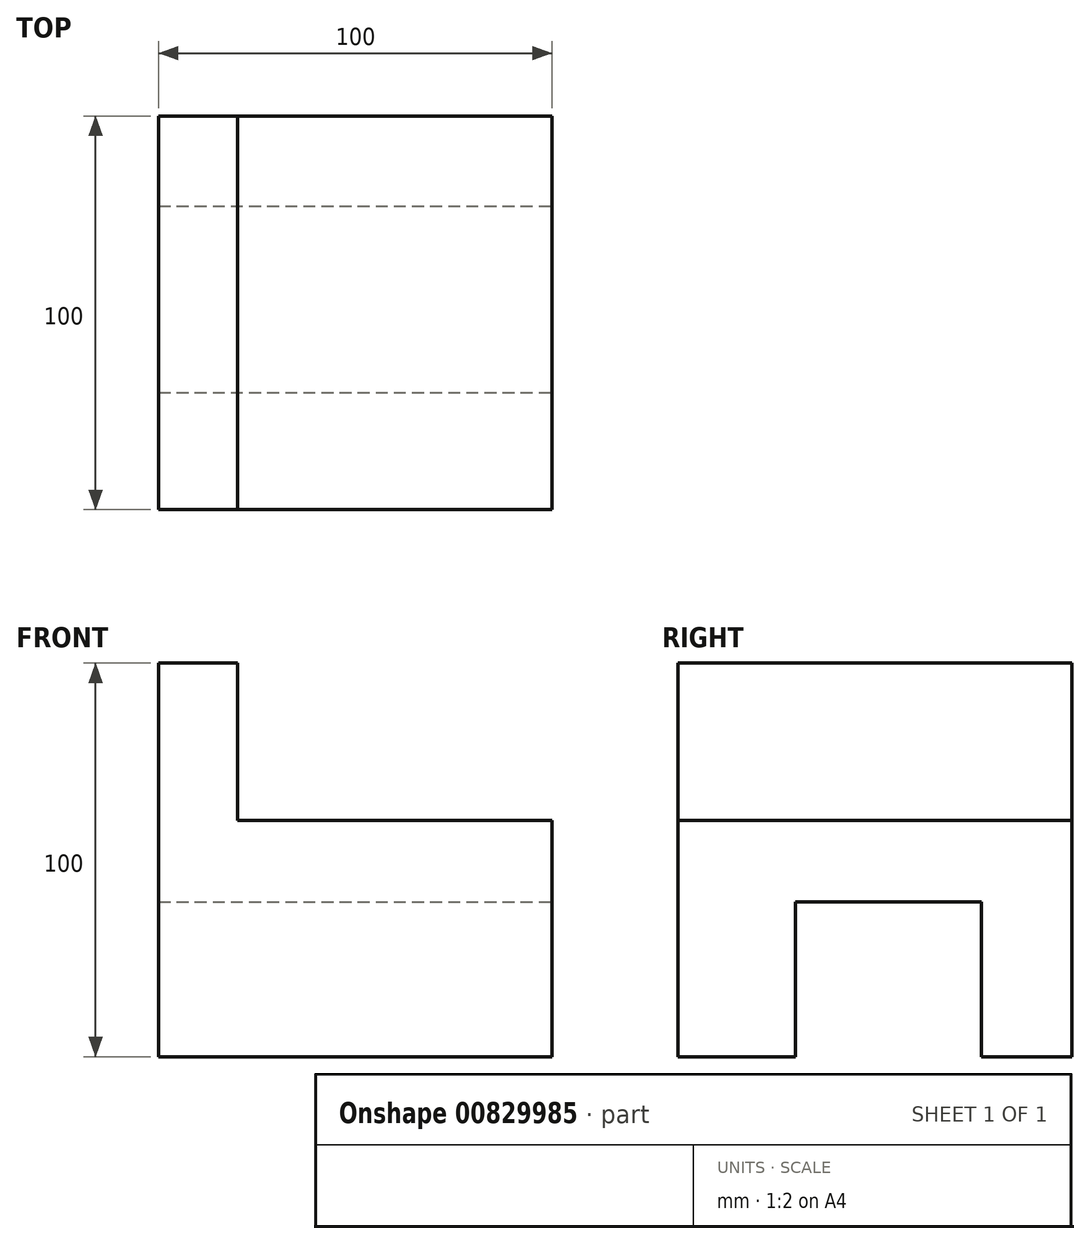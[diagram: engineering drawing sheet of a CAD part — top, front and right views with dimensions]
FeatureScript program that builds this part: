
annotation { "Feature Type Name" : "Feature", "Feature Type Description" : "" }
export const myFeature = defineFeature(function(context is Context, id is Id, definition is map)
    precondition{}
    {
        {
            var Q0;
            Q0=qCreatedBy(makeId("Top.planeOp"),FACE);
            var sketch = newSketch(context, id + "F0", { "sketchPlane" : qUnion([Q0])});
            skLineSegment(sketch, "E0.bottom", {"start": v(-50.45, 53.35) * mm, "end": v(49.55, 53.35) * mm});
            skLineSegment(sketch, "E0.top", {"start": v(-50.45, -46.65) * mm, "end": v(49.55, -46.65) * mm});
            skLineSegment(sketch, "E0.left", {"start": v(-50.45, 53.35) * mm, "end": v(-50.45, -46.65) * mm});
            skLineSegment(sketch, "E0.right", {"start": v(49.55, 53.35) * mm, "end": v(49.55, -46.65) * mm});
            skSolve(sketch);
        }
        {
            var Q0;
            Q0=makeQuery(id+"F0.imprint","IMPRINT",FACE,{"disambiguationData":[TD([[makeQuery(id+"F0.imprint","IMPRINT",EDGE,{"derivedFrom":sQuery(id+"F0.wireOp",EDGE,"E0.bottom")}),-1.0]])]});
            extrude(context, id + "F1", {"entities" : qUnion([Q0]), "depth" : 100 * mm, "offsetDistance" : 25 * mm});
        }
        {
            var Q0;
            Q0=makeQuery(id+"F1.opExtrude","CAP_FACE",FACE,{"disambiguationData":[OSD([sQuery(id+"F0.wireOp",EDGE,"E0.bottom"),sQuery(id+"F0.wireOp",EDGE,"E0.top"),sQuery(id+"F0.wireOp",EDGE,"E0.left"),sQuery(id+"F0.wireOp",EDGE,"E0.right")])],"isStart":false});
            var sketch = newSketch(context, id + "F2", { "sketchPlane" : qUnion([Q0])});
            skLineSegment(sketch, "E1.bottom", {"start": v(49.55, -46.65) * mm, "end": v(-30.45, -46.65) * mm});
            skLineSegment(sketch, "E1.top", {"start": v(49.55, 53.35) * mm, "end": v(-30.45, 53.35) * mm});
            skLineSegment(sketch, "E1.left", {"start": v(49.55, -46.65) * mm, "end": v(49.55, 53.35) * mm});
            skLineSegment(sketch, "E1.right", {"start": v(-30.45, -46.65) * mm, "end": v(-30.45, 53.35) * mm});
            skSolve(sketch);
        }
        {
            var Q0;
            Q0=makeQuery(id+"F2.imprint","IMPRINT",FACE,{"disambiguationData":[TD([[makeQuery(id+"F2.imprint","IMPRINT",EDGE,{"derivedFrom":sQuery(id+"F2.wireOp",EDGE,"E1.bottom")}),1.0]])]});
            extrude(context, id + "F3", {"entities" : qUnion([Q0]), "operationType" : NewBodyOperationType.REMOVE, "oppositeDirection" : true, "depth" : 40 * mm, "offsetDistance" : 25 * mm});
        }
        {
            var Q0;
            Q0=makeQuery(id+"F1.opExtrude","SWEPT_FACE",FACE,{"disambiguationData":[OSD([sQuery(id+"F0.wireOp",EDGE,"E0.right")])]});
            var sketch = newSketch(context, id + "F4", { "sketchPlane" : qUnion([Q0])});
            skLineSegment(sketch, "E2.bottom", {"start": v(-16.88, 39.34) * mm, "end": v(30.4, 39.34) * mm});
            skLineSegment(sketch, "E2.top", {"start": v(-16.88, 0) * mm, "end": v(30.4, 0) * mm});
            skLineSegment(sketch, "E2.left", {"start": v(-16.88, 39.34) * mm, "end": v(-16.88, 0) * mm});
            skLineSegment(sketch, "E2.right", {"start": v(30.4, 39.34) * mm, "end": v(30.4, 0) * mm});
            skSolve(sketch);
        }
        {
            var Q0;
            Q0 = qSketchRegion(id + "F4", true);
            extrude(context, id + "F5", {"entities" : qUnion([Q0]), "operationType" : NewBodyOperationType.REMOVE, "endBound" : BoundingType.THROUGH_ALL, "oppositeDirection" : true, "depth" : 25 * mm, "offsetDistance" : 25 * mm});
        }
    });
